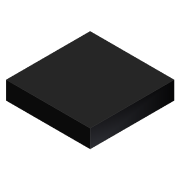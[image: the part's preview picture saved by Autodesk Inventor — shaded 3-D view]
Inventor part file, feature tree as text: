
AUTODESK INVENTOR PART (.ipt)
format: ipt  version: unknown  size: 165,888 bytes
history: native  units: mm
features: extrude x1, sketch x1
ambient origin geometry x8: Origin, YZ Plane, XZ Plane, XY Plane, X Axis, Y Axis, Z Axis, Center Point
feature tree (2):
  extrude  "Выдавливание2"  Depth=7.0mm
  sketch  "Эскиз2"
